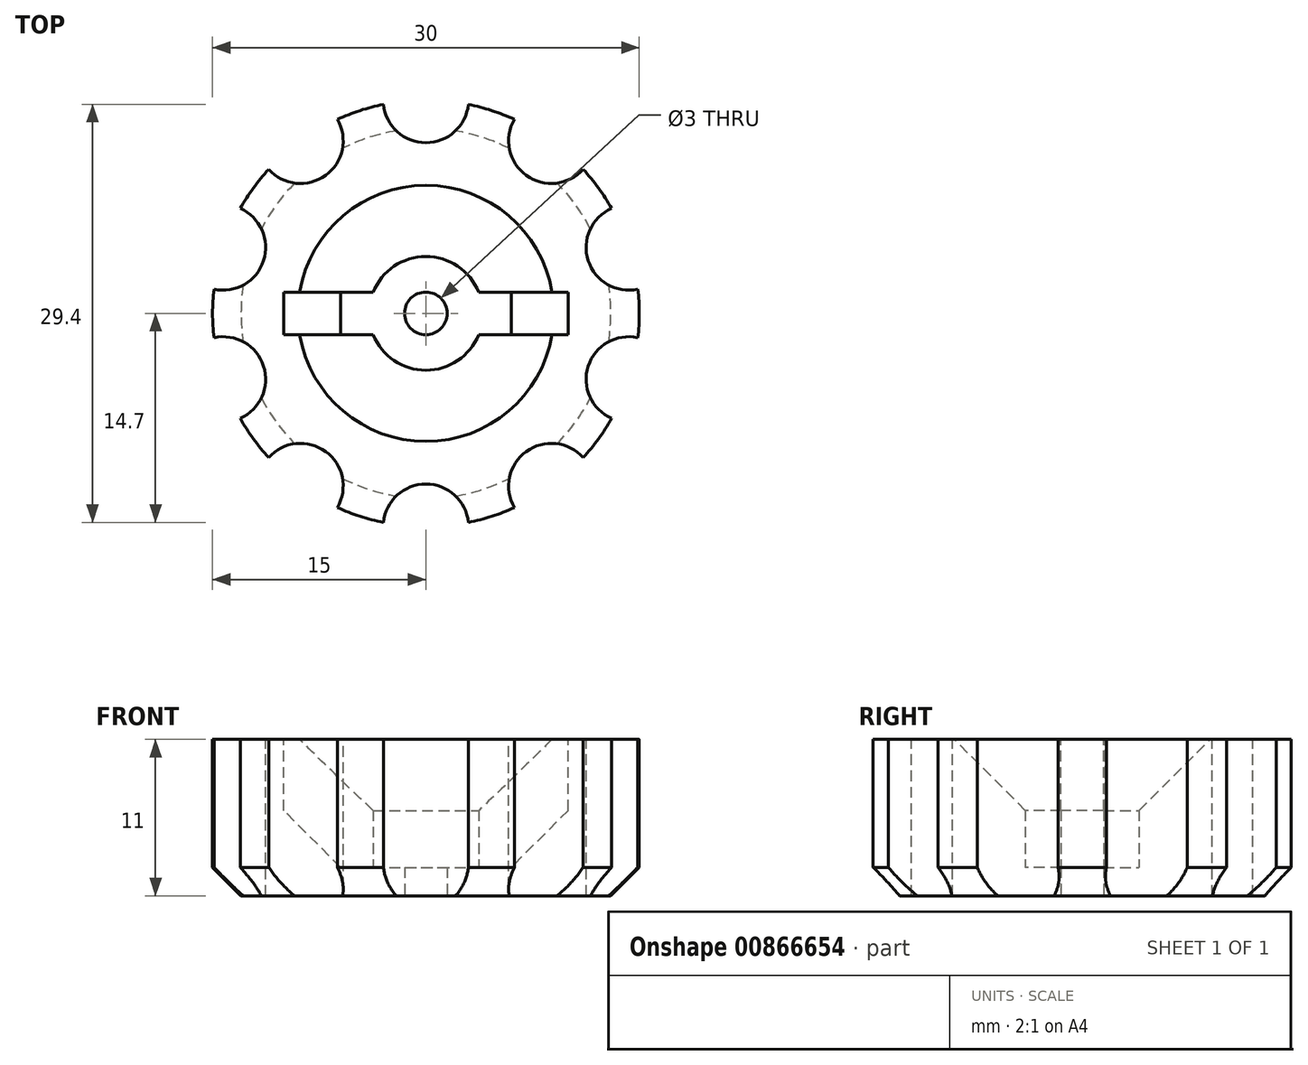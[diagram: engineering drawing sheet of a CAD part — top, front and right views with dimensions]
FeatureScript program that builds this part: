
annotation { "Feature Type Name" : "Feature", "Feature Type Description" : "" }
export const myFeature = defineFeature(function(context is Context, id is Id, definition is map)
    precondition{}
    {
        {
            var Q0;
            Q0=qCreatedBy(makeId("Front.planeOp"),FACE);
            var sketch = newSketch(context, id + "F0", { "sketchPlane" : qUnion([Q0])});
            skLineSegment(sketch, "E0.left", {"start": v(0, 0) * mm, "end": v(0, 3.42) * mm});
            skLineSegment(sketch, "E1.bottom", {"start": v(-1.5, 0) * mm, "end": v(-15, 0) * mm});
            skLineSegment(sketch, "E1.top", {"start": v(-9, 9) * mm, "end": v(-15, 9) * mm});
            skLineSegment(sketch, "E1.left", {"start": v(0, 0) * mm, "end": v(0, 9) * mm});
            skLineSegment(sketch, "E1.right", {"start": v(-15, 0) * mm, "end": v(-15, 9) * mm});
            skLineSegment(sketch, "E2.bottom", {"start": v(-1.5, 0) * mm, "end": v(-4, 0) * mm});
            skLineSegment(sketch, "E2.left", {"start": v(0, 0) * mm, "end": v(0, 4) * mm});
            skLineSegment(sketch, "E2.right", {"start": v(-4, 0) * mm, "end": v(-4, 4) * mm});
            skLineSegment(sketch, "E3.top", {"start": v(0, -2) * mm, "end": v(-13, -2) * mm});
            skLineSegment(sketch, "E4", {"start": v(-1.5, 0) * mm, "end": v(-1.5, -2) * mm});
            skLineSegment(sketch, "E5", {"start": v(-4, 4) * mm, "end": v(-9, 9) * mm});
            skLineSegment(sketch, "E6", {"start": v(-15, 0) * mm, "end": v(-13, -2) * mm});
            skPoint(sketch, "E7.orphan", {"position": v(-15, -2) * mm});
            skSolve(sketch);
        }
        {
            var Q0;
            Q0 = qSketchRegion(id + "F0", true);
            var Q1;
            Q1=sQuery(id+"F0.wireOp",EDGE,"E1.left");
            revolve(context, id + "F1", {"surfaceOperationType" : NewSurfaceOperationType.NEW, "entities" : qUnion([Q0]), "axis" : qUnion([Q1]), "revolveType" : RevolveType.FULL});
        }
        {
            var Q0;
            Q0=makeQuery(id+"F1.opRevolve","SWEPT_FACE",FACE,{"disambiguationData":[OSD([sQuery(id+"F0.wireOp",EDGE,"E1.top")])]});
            var sketch = newSketch(context, id + "F2", { "sketchPlane" : qUnion([Q0])});
            skLineSegment(sketch, "E8.bottom", {"start": v(-10, -1.5) * mm, "end": v(10, -1.5) * mm});
            skLineSegment(sketch, "E8.top", {"start": v(-10, 1.5) * mm, "end": v(10, 1.5) * mm});
            skLineSegment(sketch, "E8.left", {"start": v(-10, -1.5) * mm, "end": v(-10, 1.5) * mm});
            skLineSegment(sketch, "E8.right", {"start": v(10, -1.5) * mm, "end": v(10, 1.5) * mm});
            skPoint(sketch, "E8.middle", {"position": v(0, 0) * mm});
            skSolve(sketch);
        }
        {
            var Q0;
            Q0 = qSketchRegion(id + "F2", true);
            extrude(context, id + "F3", {"entities" : qUnion([Q0]), "operationType" : NewBodyOperationType.REMOVE, "oppositeDirection" : true, "depth" : 9 * mm, "offsetDistance" : 25 * mm});
        }
        {
            var Q0;
            Q0=makeQuery(id+"F3.boolean.opBoolean","SPLIT",FACE,{"disambiguationData":[TD([makeQuery(id+"F3.opExtrude","SWEPT_FACE",FACE,{"disambiguationData":[OSD([sQuery(id+"F2.wireOp",EDGE,"E8.bottom")])]})])],"derivedFrom":makeQuery(id+"F1.opRevolve","SWEPT_FACE",FACE,{"disambiguationData":[OSD([sQuery(id+"F0.wireOp",EDGE,"E1.top")])]})});
            var sketch = newSketch(context, id + "F4", { "sketchPlane" : qUnion([Q0])});
            skCircle(sketch, "E9", {"center": v(0, 0) * mm, "radius": 15 * mm});
            skCircle(sketch, "E10", {"center": v(0, 15) * mm, "radius": 3 * mm});
            skCircle(sketch, "E11.1.0", {"center": v(-8.82, 12.14) * mm, "radius": 3 * mm});
            skCircle(sketch, "E11.2.0", {"center": v(-14.27, 4.64) * mm, "radius": 3 * mm});
            skCircle(sketch, "E11.3.0", {"center": v(-14.27, -4.64) * mm, "radius": 3 * mm});
            skCircle(sketch, "E11.4.0", {"center": v(-8.82, -12.14) * mm, "radius": 3 * mm});
            skCircle(sketch, "E11.5.0", {"center": v(0, -15) * mm, "radius": 3 * mm});
            skCircle(sketch, "E11.6.0", {"center": v(8.82, -12.14) * mm, "radius": 3 * mm});
            skCircle(sketch, "E11.7.0", {"center": v(14.27, -4.64) * mm, "radius": 3 * mm});
            skCircle(sketch, "E11.8.0", {"center": v(14.27, 4.64) * mm, "radius": 3 * mm});
            skCircle(sketch, "E11.9.0", {"center": v(8.82, 12.14) * mm, "radius": 3 * mm});
            skSolve(sketch);
        }
        {
            var Q0;
            {var subQ0=sQuery(id+"F4.wireOp",EDGE,"E11.6.0");var subQ1=sQuery(id+"F4.wireOp",EDGE,"E9");var subQ2=makeQuery(id+"F4.imprint","INTERSECT",VERTEX,{"disambiguationData":[OD(0.0)],"derivedFrom":[subQ1,subQ0]});Q0=makeQuery(id+"F4.imprint","IMPRINT",FACE,{"disambiguationData":[TD([[makeQuery(id+"F4.imprint","IMPRINT",EDGE,{"disambiguationData":[TD([[subQ2,-1.0]])],"derivedFrom":subQ1}),-1.0]])]});}
            var Q1;
            {var subQ0=sQuery(id+"F4.wireOp",EDGE,"E11.5.0");var subQ1=sQuery(id+"F4.wireOp",EDGE,"E9");var subQ2=makeQuery(id+"F4.imprint","INTERSECT",VERTEX,{"disambiguationData":[OD(0.0)],"derivedFrom":[subQ1,subQ0]});Q1=makeQuery(id+"F4.imprint","IMPRINT",FACE,{"disambiguationData":[TD([[makeQuery(id+"F4.imprint","IMPRINT",EDGE,{"disambiguationData":[TD([[subQ2,-1.0]])],"derivedFrom":subQ1}),-1.0]])]});}
            var Q2;
            {var subQ0=sQuery(id+"F4.wireOp",EDGE,"E11.4.0");var subQ1=sQuery(id+"F4.wireOp",EDGE,"E9");var subQ2=makeQuery(id+"F4.imprint","INTERSECT",VERTEX,{"disambiguationData":[OD(0.0)],"derivedFrom":[subQ1,subQ0]});Q2=makeQuery(id+"F4.imprint","IMPRINT",FACE,{"disambiguationData":[TD([[makeQuery(id+"F4.imprint","IMPRINT",EDGE,{"disambiguationData":[TD([[subQ2,-1.0]])],"derivedFrom":subQ1}),-1.0]])]});}
            var Q3;
            {var subQ0=sQuery(id+"F4.wireOp",EDGE,"E11.3.0");var subQ1=sQuery(id+"F4.wireOp",EDGE,"E9");var subQ2=makeQuery(id+"F4.imprint","INTERSECT",VERTEX,{"disambiguationData":[OD(0.0)],"derivedFrom":[subQ1,subQ0]});Q3=makeQuery(id+"F4.imprint","IMPRINT",FACE,{"disambiguationData":[TD([[makeQuery(id+"F4.imprint","IMPRINT",EDGE,{"disambiguationData":[TD([[subQ2,-1.0]])],"derivedFrom":subQ1}),-1.0]])]});}
            var Q4;
            {var subQ0=sQuery(id+"F4.wireOp",EDGE,"E11.2.0");var subQ1=sQuery(id+"F4.wireOp",EDGE,"E9");var subQ2=makeQuery(id+"F4.imprint","INTERSECT",VERTEX,{"disambiguationData":[OD(0.0)],"derivedFrom":[subQ1,subQ0]});Q4=makeQuery(id+"F4.imprint","IMPRINT",FACE,{"disambiguationData":[TD([[makeQuery(id+"F4.imprint","IMPRINT",EDGE,{"disambiguationData":[TD([[subQ2,1.0]])],"derivedFrom":subQ1}),-1.0]])]});}
            var Q5;
            {var subQ0=sQuery(id+"F4.wireOp",EDGE,"E11.1.0");var subQ1=sQuery(id+"F4.wireOp",EDGE,"E9");var subQ2=makeQuery(id+"F4.imprint","INTERSECT",VERTEX,{"disambiguationData":[OD(0.0)],"derivedFrom":[subQ1,subQ0]});Q5=makeQuery(id+"F4.imprint","IMPRINT",FACE,{"disambiguationData":[TD([[makeQuery(id+"F4.imprint","IMPRINT",EDGE,{"disambiguationData":[TD([[subQ2,-1.0]])],"derivedFrom":subQ1}),-1.0]])]});}
            var Q6;
            {var subQ0=sQuery(id+"F4.wireOp",EDGE,"E10");var subQ1=sQuery(id+"F4.wireOp",EDGE,"E9");var subQ2=makeQuery(id+"F4.imprint","INTERSECT",VERTEX,{"disambiguationData":[OD(0.0)],"derivedFrom":[subQ1,subQ0]});Q6=makeQuery(id+"F4.imprint","IMPRINT",FACE,{"disambiguationData":[TD([[makeQuery(id+"F4.imprint","IMPRINT",EDGE,{"disambiguationData":[TD([[subQ2,-1.0]])],"derivedFrom":subQ1}),-1.0]])]});}
            var Q7;
            {var subQ0=sQuery(id+"F4.wireOp",EDGE,"E11.9.0");var subQ1=sQuery(id+"F4.wireOp",EDGE,"E9");var subQ2=makeQuery(id+"F4.imprint","INTERSECT",VERTEX,{"disambiguationData":[OD(0.0)],"derivedFrom":[subQ1,subQ0]});Q7=makeQuery(id+"F4.imprint","IMPRINT",FACE,{"disambiguationData":[TD([[makeQuery(id+"F4.imprint","IMPRINT",EDGE,{"disambiguationData":[TD([[subQ2,-1.0]])],"derivedFrom":subQ1}),-1.0]])]});}
            var Q8;
            {var subQ0=sQuery(id+"F4.wireOp",EDGE,"E11.8.0");var subQ1=sQuery(id+"F4.wireOp",EDGE,"E9");var subQ2=makeQuery(id+"F4.imprint","INTERSECT",VERTEX,{"disambiguationData":[OD(0.0)],"derivedFrom":[subQ1,subQ0]});Q8=makeQuery(id+"F4.imprint","IMPRINT",FACE,{"disambiguationData":[TD([[makeQuery(id+"F4.imprint","IMPRINT",EDGE,{"disambiguationData":[TD([[subQ2,-1.0]])],"derivedFrom":subQ1}),-1.0]])]});}
            var Q9;
            {var subQ0=sQuery(id+"F4.wireOp",EDGE,"E11.7.0");var subQ1=sQuery(id+"F4.wireOp",EDGE,"E9");var subQ2=makeQuery(id+"F4.imprint","INTERSECT",VERTEX,{"disambiguationData":[OD(0.0)],"derivedFrom":[subQ1,subQ0]});Q9=makeQuery(id+"F4.imprint","IMPRINT",FACE,{"disambiguationData":[TD([[makeQuery(id+"F4.imprint","IMPRINT",EDGE,{"disambiguationData":[TD([[subQ2,-1.0]])],"derivedFrom":subQ1}),-1.0]])]});}
            extrude(context, id + "F5", {"entities" : qUnion([Q0, Q1, Q2, Q3, Q4, Q5, Q6, Q7, Q8, Q9]), "operationType" : NewBodyOperationType.REMOVE, "oppositeDirection" : true, "depth" : 25 * mm, "offsetDistance" : 25 * mm});
        }
        {
            var Q0;
            Q0=makeQuery(id+"F3.boolean.opBoolean","COPY",EDGE,{"derivedFrom":makeQuery(id+"F3.opExtrude","CAP_EDGE",EDGE,{"disambiguationData":[OSD([sQuery(id+"F2.wireOp",EDGE,"E8.right")])],"isStart":false})});
            var Q1;
            Q1=makeQuery(id+"F3.boolean.opBoolean","COPY",EDGE,{"derivedFrom":makeQuery(id+"F3.opExtrude","CAP_EDGE",EDGE,{"disambiguationData":[OSD([sQuery(id+"F2.wireOp",EDGE,"E8.left")])],"isStart":false})});
            chamfer(context, id + "F6", {"entities" : qUnion([Q0, Q1]), "width" : 4 * mm, "tangentPropagation" : true});
        }
    });
